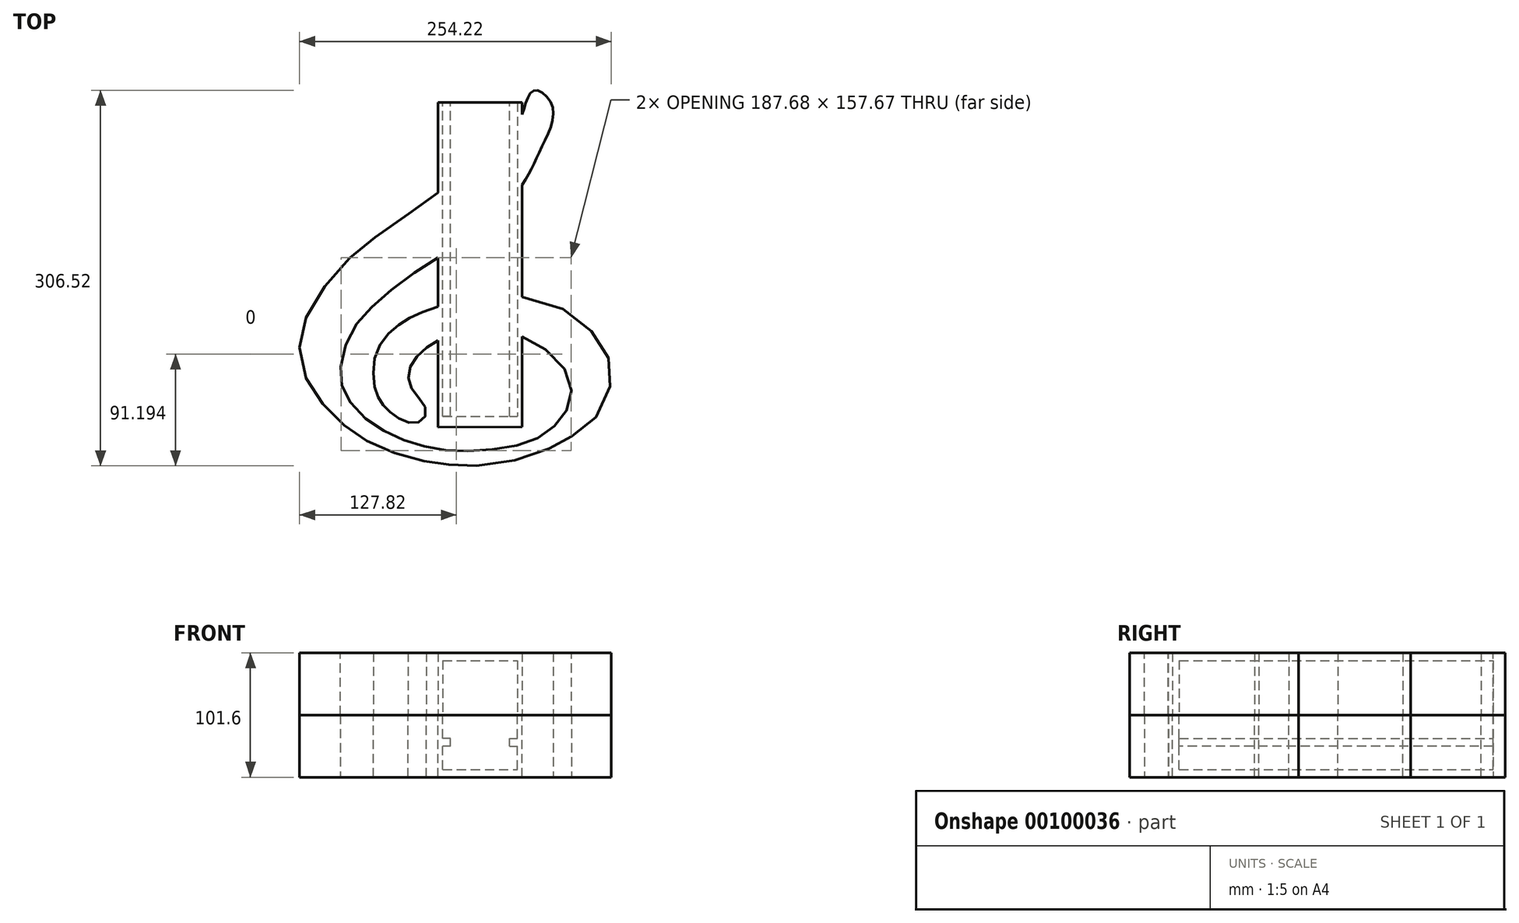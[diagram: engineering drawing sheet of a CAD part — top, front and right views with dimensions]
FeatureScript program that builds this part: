
annotation { "Feature Type Name" : "Feature", "Feature Type Description" : "" }
export const myFeature = defineFeature(function(context is Context, id is Id, definition is map)
    precondition{}
    {
        {
            var Q0;
            Q0=qCreatedBy(makeId("Top.planeOp"),FACE);
            var sketch = newSketch(context, id + "F0", { "sketchPlane" : qUnion([Q0])});
            skFitSpline(sketch, "E0", {"points": [v(39.3, 181.59) * mm, v(29.93, 162.26) * mm, v(23.76, 150.6) * mm, v(16.45, 141.23) * mm, v(5.7, 130.95) * mm, v(-1.56, 124.93) * mm, v(-15.18, 114.48) * mm, v(-31.88, 103.03) * mm, v(-46.47, 92.91) * mm, v(-82.14, 67.46) * mm, v(-103.67, 51.5) * mm, v(-126.33, 28.2) * mm, v(-144.75, 0) * mm, v(-151.54, -22.45) * mm, v(-148.7, -46.93) * mm, v(-138.58, -66.92) * mm, v(-123, -84.7) * mm, v(-107.62, -97.52) * mm, v(-91.88, -106.7) * mm, v(-70.6, -115.36) * mm, v(-49.08, -120.97) * mm, v(-33.55, -123.4) * mm, v(-18.64, -124.48) * mm, v(9.74, -123.21) * mm, v(46.2, -113.07) * mm, v(62.12, -105.37) * mm, v(78.39, -94.98) * mm, v(95.38, -77.5) * mm, v(102.46, -50.85) * mm, v(98.91, -33.4) * mm, v(83.72, -12.14) * mm, v(56.57, 6.23) * mm, v(12.85, 14.9) * mm, v(-18.27, 11.13) * mm, v(-53.62, 0) * mm, v(-73.8, -11.8) * mm, v(-89.05, -31.76) * mm, v(-90.73, -58.68) * mm, v(-85.69, -72.14) * mm, v(-77.15, -81.3) * mm, v(-63.81, -88.96) * mm, v(-52.04, -87.7) * mm, v(-48.67, -78.03) * mm, v(-58.35, -64.57) * mm, v(-62.97, -49) * mm, v(-53.3, -32.6) * mm, v(-33.95, -20.4) * mm, v(-11.37, -15.15) * mm, v(11.53, -14.66) * mm, v(32.97, -20.51) * mm, v(60.7, -40.39) * mm, v(70.09, -64.1) * mm, v(64.48, -82.14) * mm, v(52.33, -95.36) * mm, v(34.31, -105.63) * mm, v(8.21, -110.92) * mm, v(-19.61, -112.64) * mm, v(-41.05, -110.52) * mm, v(-61.74, -105.31) * mm, v(-81.87, -96.7) * mm, v(-100.35, -83.9) * mm, v(-113.97, -67.42) * mm, v(-118.19, -53.37) * mm, v(-116.51, -33.34) * mm, v(-105.9, -9.9) * mm, v(-89.74, 7.86) * mm, v(-62.08, 30.05) * mm, v(-31.37, 49.84) * mm, v(-6.38, 65.83) * mm, v(10.75, 81.1) * mm, v(32.67, 109.01) * mm, v(45.32, 134.6) * mm, v(54.61, 168.66) * mm, v(39.3, 181.59) * mm]});
            skPoint(sketch, "E1", {"position": v(32.22, 169.88) * mm});
            skPoint(sketch, "E2", {"position": v(34.31, -117.25) * mm});
            skLineSegment(sketch, "E3", {"start": v(-40.98, 173.02) * mm, "end": v(22.52, 173.02) * mm, "construction": true});
            skSolve(sketch);
        }
        {
            var Q0;
            Q0=qSketchRegion(id+"F0",true);
            extrude(context, id + "F1", {"entities" : qUnion([Q0]), "depth" : 50.8 * mm});
        }
        {
            var Q0;
            Q0=makeQuery(id+"F1.opExtrude","CAP_FACE",FACE,{"disambiguationData":[OSD([sQuery(id+"F0.wireOp",EDGE,"E0")])],"isStart":false});
            var sketch = newSketch(context, id + "F2", { "sketchPlane" : qUnion([Q0])});
            skLineSegment(sketch, "E4.bottom", {"start": v(29.89, -12.84) * mm, "end": v(-38.7, -12.84) * mm});
            skLineSegment(sketch, "E4.top", {"start": v(29.89, 634.86) * mm, "end": v(-38.7, 634.86) * mm});
            skLineSegment(sketch, "E4.left", {"start": v(29.89, -12.84) * mm, "end": v(29.89, 634.86) * mm});
            skLineSegment(sketch, "E4.right", {"start": v(-38.7, -12.84) * mm, "end": v(-38.7, 634.86) * mm});
            skLineSegment(sketch, "E5.bottom", {"start": v(-38.7, -12.84) * mm, "end": v(22.52, -12.84) * mm});
            skPoint(sketch, "E6", {"position": v(-38.7, -93.1) * mm});
            skLineSegment(sketch, "E7", {"start": v(-38.7, -12.84) * mm, "end": v(-38.7, -93.1) * mm});
            skLineSegment(sketch, "E8", {"start": v(29.89, -12.84) * mm, "end": v(29.89, -92.95) * mm});
            skLineSegment(sketch, "E9", {"start": v(29.89, -92.95) * mm, "end": v(-38.7, -93.1) * mm});
            skPoint(sketch, "E10", {"position": v(29.89, 171.87) * mm});
            skPoint(sketch, "E11", {"position": v(-38.7, 171.87) * mm});
            skLineSegment(sketch, "E12", {"start": v(-38.7, 171.87) * mm, "end": v(29.89, 171.87) * mm});
            skSolve(sketch);
        }
        {
            var Q0;
            {var subQ0=sQuery(id+"F2.wireOp",EDGE,"E12");Q0=makeQuery(id+"F2.imprint","IMPRINT",FACE,{"disambiguationData":[TD([[makeQuery(id+"F2.imprint","IMPRINT",EDGE,{"derivedFrom":subQ0}),-1.0]])]});}
            var Q1;
            {var subQ0=sQuery(id+"F2.wireOp",EDGE,"E4.left");var subQ1=makeQuery(id+"F1.opExtrude","CAP_EDGE",EDGE,{"disambiguationData":[OSD([sQuery(id+"F0.wireOp",EDGE,"E0")])],"isStart":false});var subQ2=makeQuery(id+"F2.imprint","INTERSECT",VERTEX,{"disambiguationData":[OD(1.0)],"derivedFrom":[subQ1,subQ0]});Q1=makeQuery(id+"F2.imprint","IMPRINT",FACE,{"disambiguationData":[TD([[makeQuery(id+"F2.imprint","IMPRINT",EDGE,{"disambiguationData":[TD([[subQ2,-1.0]])],"derivedFrom":subQ0}),1.0]])]});}
            var Q2;
            {var subQ6=sQuery(id+"F2.wireOp",EDGE,"E4.bottom");Q2=makeQuery(id+"F2.imprint","IMPRINT",FACE,{"disambiguationData":[TD([[makeQuery(id+"F2.imprint","IMPRINT",EDGE,{"derivedFrom":subQ6}),-1.0]])]});}
            var Q3;
            {var subQ1=sQuery(id+"F2.wireOp",EDGE,"E4.bottom");Q3=makeQuery(id+"F2.imprint","IMPRINT",FACE,{"disambiguationData":[TD([[makeQuery(id+"F2.imprint","IMPRINT",EDGE,{"derivedFrom":subQ1}),1.0]])]});}
            var Q4;
            {var subQ0=sQuery(id+"F2.wireOp",EDGE,"E9");Q4=makeQuery(id+"F2.imprint","IMPRINT",FACE,{"disambiguationData":[TD([[makeQuery(id+"F2.imprint","IMPRINT",EDGE,{"derivedFrom":subQ0}),-1.0]])]});}
            var Q5;
            {var subQ0=sQuery(id+"F2.wireOp",EDGE,"E7");var subQ1=makeQuery(id+"F1.opExtrude","CAP_EDGE",EDGE,{"disambiguationData":[OSD([sQuery(id+"F0.wireOp",EDGE,"E0")])],"isStart":false});var subQ2=makeQuery(id+"F2.imprint","INTERSECT",VERTEX,{"disambiguationData":[OD(1.0)],"derivedFrom":[subQ1,subQ0]});Q5=makeQuery(id+"F2.imprint","IMPRINT",FACE,{"disambiguationData":[TD([[makeQuery(id+"F2.imprint","IMPRINT",EDGE,{"disambiguationData":[TD([[subQ2,-1.0]])],"derivedFrom":subQ0}),1.0]])]});}
            var Q6;
            {var subQ1=makeQuery(id+"F1.opExtrude","CAP_EDGE",EDGE,{"disambiguationData":[OSD([sQuery(id+"F0.wireOp",EDGE,"E0")])],"isStart":false});var subQ4=sQuery(id+"F2.wireOp",EDGE,"E7");var subQ8=makeQuery(id+"F2.imprint","INTERSECT",VERTEX,{"disambiguationData":[OD(0.0)],"derivedFrom":[subQ1,subQ4]});Q6=makeQuery(id+"F2.imprint","IMPRINT",FACE,{"disambiguationData":[TD([[makeQuery(id+"F2.imprint","IMPRINT",EDGE,{"disambiguationData":[TD([[subQ8,-1.0]])],"derivedFrom":subQ4}),1.0]])]});}
            var Q7;
            {var subQ0=sQuery(id+"F2.wireOp",EDGE,"E4.left");var subQ1=makeQuery(id+"F1.opExtrude","CAP_EDGE",EDGE,{"disambiguationData":[OSD([sQuery(id+"F0.wireOp",EDGE,"E0")])],"isStart":false});var subQ2=makeQuery(id+"F2.imprint","INTERSECT",VERTEX,{"disambiguationData":[OD(0.0)],"derivedFrom":[subQ1,subQ0]});Q7=makeQuery(id+"F2.imprint","IMPRINT",FACE,{"disambiguationData":[TD([[makeQuery(id+"F2.imprint","IMPRINT",EDGE,{"disambiguationData":[TD([[subQ2,-1.0]])],"derivedFrom":subQ0}),1.0]])]});}
            extrude(context, id + "F3", {"entities" : qUnion([Q0, Q1, Q2, Q3, Q4, Q5, Q6, Q7]), "operationType" : NewBodyOperationType.ADD, "oppositeDirection" : true, "depth" : 50.8 * mm});
        }
        {
            var Q0;
            Q0=makeQuery(id+"F3.boolean.opBoolean","MERGE",FACE,{"derivedFrom":[makeQuery(id+"F1.opExtrude","CAP_FACE",FACE,{"disambiguationData":[OSD([sQuery(id+"F0.wireOp",EDGE,"E0")])],"isStart":true}),makeQuery(id+"F3.opExtrude","CAP_FACE",FACE,{"disambiguationData":[OSD([sQuery(id+"F2.wireOp",EDGE,"E4.left"),sQuery(id+"F2.wireOp",EDGE,"E4.right"),sQuery(id+"F2.wireOp",EDGE,"E7"),sQuery(id+"F2.wireOp",EDGE,"E8"),sQuery(id+"F2.wireOp",EDGE,"E9"),sQuery(id+"F2.wireOp",EDGE,"E12")])],"isStart":false})]});
            var sketch = newSketch(context, id + "F4", { "sketchPlane" : qUnion([Q0])});
            skLineSegment(sketch, "E13", {"start": v(-35, 84.13) * mm, "end": v(25.97, 84.13) * mm});
            skLineSegment(sketch, "E14", {"start": v(25.97, 84.13) * mm, "end": v(25.97, -171.87) * mm});
            skLineSegment(sketch, "E15", {"start": v(25.97, -171.87) * mm, "end": v(-35, -171.87) * mm});
            skLineSegment(sketch, "E16", {"start": v(-35, -171.87) * mm, "end": v(-35, 84.13) * mm});
            skSolve(sketch);
        }
        {
            var Q0;
            Q0=makeQuery(id+"F4.imprint","IMPRINT",FACE,{"disambiguationData":[TD([[makeQuery(id+"F4.imprint","IMPRINT",EDGE,{"derivedFrom":sQuery(id+"F4.wireOp",EDGE,"E13")}),-1.0]])]});
            extrude(context, id + "F5", {"entities" : qUnion([Q0]), "operationType" : NewBodyOperationType.REMOVE, "oppositeDirection" : true, "depth" : 44.45 * mm});
        }
        {
            var Q0;
            Q0=makeQuery(id+"F1.opExtrude","SWEPT_BODY",BODY,{"disambiguationData":[OSD([sQuery(id+"F0.wireOp",EDGE,"E0")])]});
            var Q1;
            Q1=qCreatedBy(makeId("Top.planeOp"),FACE);
            mirror(context, id + "F6", {"entities" : qUnion([Q0]), "mirrorPlane" : qUnion([Q1])});
        }
        {
            var Q0;
            Q0=makeQuery(id+"F6.opPattern","COPY",FACE,{"derivedFrom":makeQuery(id+"F5.boolean.opBoolean","COPY",FACE,{"derivedFrom":makeQuery(id+"F5.opExtrude","SWEPT_FACE",FACE,{"disambiguationData":[OSD([sQuery(id+"F4.wireOp",EDGE,"E16")])]})}),"instanceName":"1"});
            var sketch = newSketch(context, id + "F7", { "sketchPlane" : qUnion([Q0])});
            skLineSegment(sketch, "E17", {"start": v(48.27, -25.4) * mm, "end": v(171.87, -25.4) * mm});
            skPoint(sketch, "E17.endSnap0", {"position": v(171.87, -22.23) * mm});
            skLineSegment(sketch, "E18", {"start": v(48.27, -19.05) * mm, "end": v(171.87, -19.05) * mm});
            skLineSegment(sketch, "E19", {"start": v(171.87, -25.4) * mm, "end": v(171.87, -19.05) * mm});
            skLineSegment(sketch, "E20", {"start": v(48.27, -19.05) * mm, "end": v(-84.13, -19.05) * mm});
            skPoint(sketch, "E20.endSnap0", {"position": v(-84.13, -22.23) * mm});
            skLineSegment(sketch, "E21", {"start": v(-84.13, -19.05) * mm, "end": v(-84.13, -25.4) * mm});
            skLineSegment(sketch, "E22", {"start": v(-84.13, -25.4) * mm, "end": v(48.27, -25.4) * mm});
            skLineSegment(sketch, "E23", {"start": v(171.87, -25.4) * mm, "end": v(171.87, -44.45) * mm, "construction": true});
            skLineSegment(sketch, "E24", {"start": v(171.87, -19.05) * mm, "end": v(171.87, 0) * mm, "construction": true});
            skSolve(sketch);
        }
        {
            var Q0;
            Q0=makeQuery(id+"F7.imprint","IMPRINT",FACE,{"disambiguationData":[TD([[makeQuery(id+"F7.imprint","IMPRINT",EDGE,{"derivedFrom":sQuery(id+"F7.wireOp",EDGE,"E17")}),1.0]])]});
            extrude(context, id + "F8", {"entities" : qUnion([Q0]), "operationType" : NewBodyOperationType.ADD, "depth" : 6.35 * mm});
        }
        {
            var Q0;
            Q0=makeQuery(id+"F6.opPattern","COPY",FACE,{"derivedFrom":makeQuery(id+"F5.boolean.opBoolean","COPY",FACE,{"derivedFrom":makeQuery(id+"F5.opExtrude","SWEPT_FACE",FACE,{"disambiguationData":[OSD([sQuery(id+"F4.wireOp",EDGE,"E14")])]})}),"instanceName":"1"});
            var sketch = newSketch(context, id + "F9", { "sketchPlane" : qUnion([Q0])});
            skLineSegment(sketch, "E25", {"start": v(-100.33, 0) * mm, "end": v(-100.33, -19.05) * mm});
            skLineSegment(sketch, "E26", {"start": v(-100.33, -25.4) * mm, "end": v(84.13, -25.4) * mm});
            skLineSegment(sketch, "E27", {"start": v(84.13, -25.4) * mm, "end": v(84.13, -19.05) * mm});
            skLineSegment(sketch, "E28", {"start": v(84.13, -19.05) * mm, "end": v(-100.33, -19.05) * mm});
            skLineSegment(sketch, "E29", {"start": v(-100.33, -19.05) * mm, "end": v(-171.87, -19.05) * mm});
            skLineSegment(sketch, "E30", {"start": v(-171.87, -19.05) * mm, "end": v(-171.87, -25.4) * mm});
            skLineSegment(sketch, "E31", {"start": v(-171.87, -25.4) * mm, "end": v(-100.33, -25.4) * mm});
            skSolve(sketch);
        }
        {
            var Q0;
            Q0=makeQuery(id+"F9.imprint","IMPRINT",FACE,{"disambiguationData":[TD([[makeQuery(id+"F9.imprint","IMPRINT",EDGE,{"derivedFrom":sQuery(id+"F9.wireOp",EDGE,"E26")}),1.0]])]});
            extrude(context, id + "F10", {"entities" : qUnion([Q0]), "operationType" : NewBodyOperationType.ADD, "depth" : 6.35 * mm});
        }
    });
